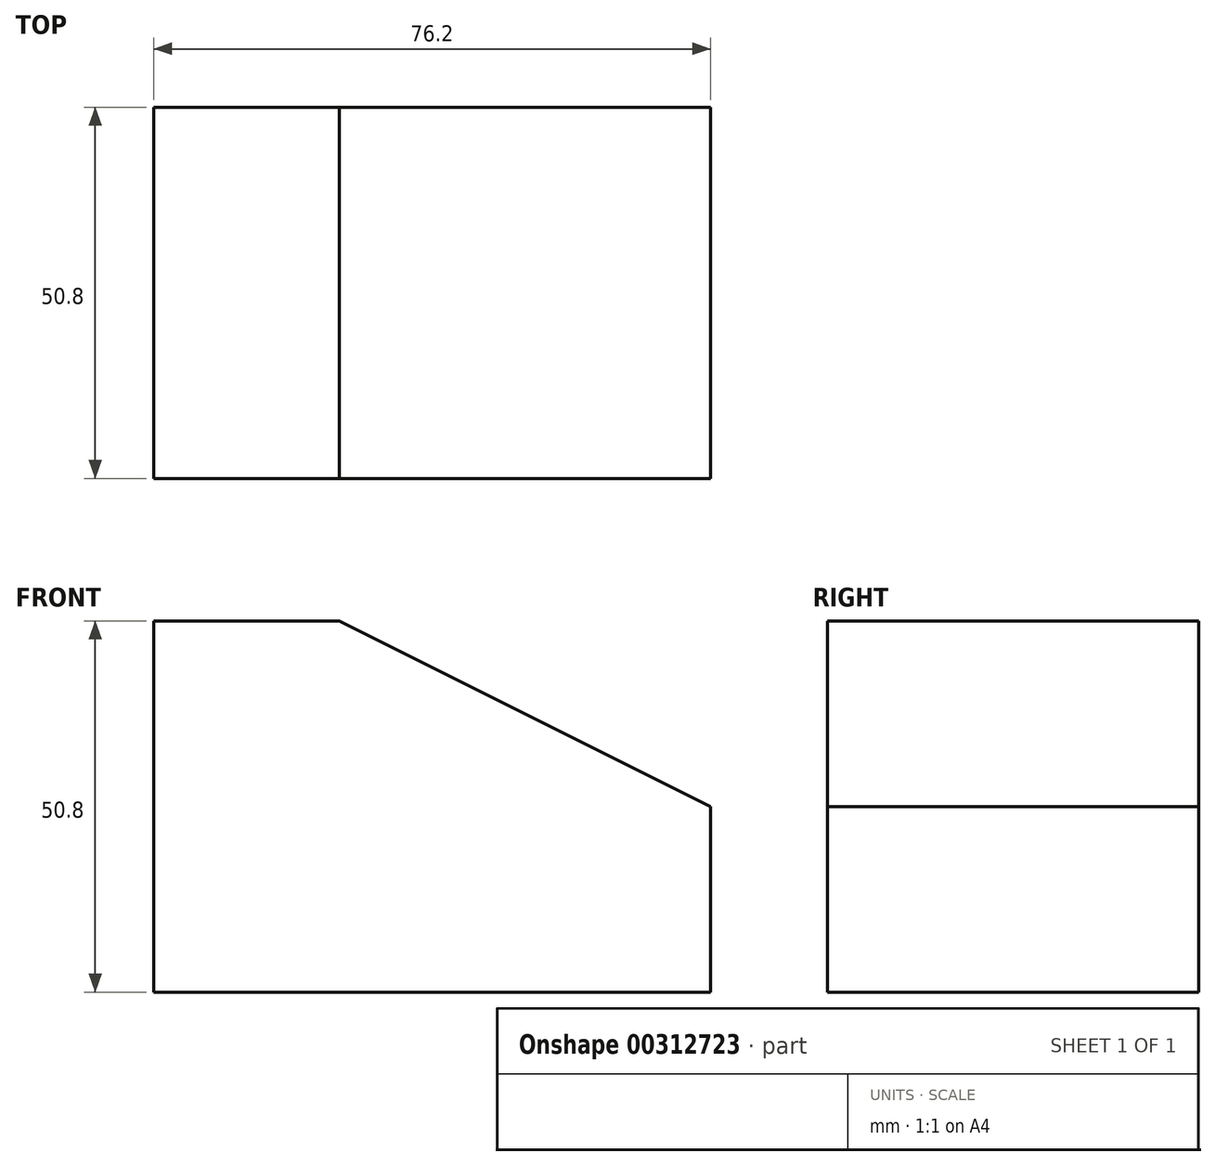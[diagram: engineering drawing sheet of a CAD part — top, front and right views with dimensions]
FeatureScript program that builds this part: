
annotation { "Feature Type Name" : "Feature", "Feature Type Description" : "" }
export const myFeature = defineFeature(function(context is Context, id is Id, definition is map)
    precondition{}
    {
        {
            var Q0;
            Q0=qCreatedBy(makeId("Front.planeOp"),FACE);
            var sketch = newSketch(context, id + "F0", { "sketchPlane" : qUnion([Q0])});
            skLineSegment(sketch, "E0", {"start": v(-57.69, 22.55) * mm, "end": v(-57.69, -28.25) * mm});
            skLineSegment(sketch, "E1", {"start": v(-57.69, -28.25) * mm, "end": v(18.51, -28.25) * mm});
            skLineSegment(sketch, "E2", {"start": v(18.51, -28.25) * mm, "end": v(18.51, -2.85) * mm});
            skLineSegment(sketch, "E3", {"start": v(-57.69, 22.55) * mm, "end": v(-32.29, 22.55) * mm});
            skLineSegment(sketch, "E4", {"start": v(-32.29, 22.55) * mm, "end": v(18.51, -2.85) * mm});
            skSolve(sketch);
        }
        {
            var Q0;
            Q0=makeQuery(id+"F0.imprint","IMPRINT",FACE,{"disambiguationData":[TD([[makeQuery(id+"F0.imprint","IMPRINT",EDGE,{"derivedFrom":sQuery(id+"F0.wireOp",EDGE,"E0")}),1.0]])]});
            extrude(context, id + "F1", {"entities" : qUnion([Q0]), "depth" : 50.8 * mm});
        }
    });
